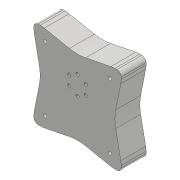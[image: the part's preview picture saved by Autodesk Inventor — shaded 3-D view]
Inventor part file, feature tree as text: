
AUTODESK INVENTOR PART (.ipt)
format: ipt  version: 2018 (Build 220112000, 112)  size: 1,824,768 bytes
history: native  units: mm
features: sketch x42, projected_geometry x36, extrude x34, fillet x9, hole x6, chamfer x5, other x2, pattern_circular x2, mirror x1, revolve x1, shell x1, plane x1, loft x1
ambient origin geometry x8: Origin, YZ Plane, XZ Plane, XY Plane, X Axis, Y Axis, Z Axis, Center Point
bodies: Solid1 (feature_tree), Solid2 (feature_tree)
feature tree (141):
  extrude  "Extrusion1"  Depth=45.0mm
  extrude  "Extrusion2"  Depth=2.25mm
  hole  "Hole1"  [1 undecoded]
  hole  "Hole2"  [1 undecoded]
  fillet  "Fillet1"  Radius=14.0mm
  extrude  "Extrusion3"  Depth=18.5mm
  extrude  "Extrusion4"  Depth=10.0mm
  extrude  "Extrusion5"  Depth=2.195mm
  extrude  "Extrusion6"  Depth=20.5mm
  hole  "Hole3"  [1 undecoded]
  extrude  "Extrusion7"  Depth=0.5mm
  extrude  "Extrusion8"  Depth=5.0mm TaperAngle=0.0deg
  extrude  "Extrusion9"  Depth=10.0mm
  extrude  "Extrusion10"  Depth=10.0mm
  extrude  "Extrusion11"  Depth=14.5mm
  extrude  "Extrusion12"  Depth=14.5mm
  extrude  "Extrusion13"  Depth=5.0mm
  extrude  "Extrusion14"  Depth=2.25mm
  extrude  "Extrusion15"  Depth=5.0mm
  extrude  "Extrusion16"  Depth=9.0mm
  extrude  "Extrusion17"  Depth=4.0mm
  chamfer  "Chamfer1"  Distance=1.0mm
  fillet  "Fillet7"  Radius=20.7mm
  fillet  "Fillet8"  Radius=32.0mm
  mirror  "Mirror1"
  extrude  "Extrusion18"  Depth=1.0mm TaperAngle=0.0deg
  extrude  "Extrusion19"  Depth=8.0mm
  extrude  "Extrusion20"  Depth=0.2mm TaperAngle=0.0deg
  extrude  "Extrusion21"  Depth=0.5mm TaperAngle=0.0deg
  extrude  "Extrusion22"  Depth=3.0mm TaperAngle=0.0deg
  extrude  "Extrusion23"  Depth=0.2mm TaperAngle=0.0deg
  extrude  "Extrusion24"  Depth=2.5mm TaperAngle=45.0deg
  sketch  "Sketch35"  dims[d91=8.0mm d92=0.0mm d93=3.0mm d94=0.0mm]
  other  "Work Axis1"
  revolve  "Revolution1"  [1 undecoded]
  extrude  "Extrusion25"  Depth=4.0mm TaperAngle=0.0deg
  extrude  "Extrusion26"  Depth=19.2mm TaperAngle=0.0deg
  shell  "Shell1"  Thickness=52.1mm
  extrude  "Extrusion27"  Depth=9.0mm
  extrude  "Extrusion28"  Depth=25.0mm
  chamfer  "Chamfer4"  Distance=6.9mm
  chamfer  "Chamfer5"  Distance=2.5mm
  extrude  "Extrusion29"  TaperAngle=90.0deg  [1 undecoded]
  pattern_circular  "Circular Pattern1"  [2 undecoded]
  fillet  "Fillet11"  Radius=5.0mm
  fillet  "Fillet12"  Radius=12.8mm
  fillet  "Fillet13"  Radius=12.8mm
  fillet  "Fillet14"  Radius=12.8mm
  chamfer  "Chamfer6"  Distance=12.8mm
  hole  "Hole6"  [1 undecoded]
  extrude  "Extrusion30"  Depth=25.0mm
  fillet  "Fillet15"  Radius=20.0mm
  extrude  "Extrusion31"  Depth=25.0mm
  plane  "Work Plane1"
  loft  "Loft1"
  hole  "Hole8"  [1 undecoded]
  extrude  "Extrusion35"  Depth=25.0mm TaperAngle=0.0deg
  chamfer  "Chamfer7"  Distance=40.0mm
  fillet  "Fillet20"  Radius=5.1mm
  extrude  "Extrusion36"  Depth=25.0mm TaperAngle=45.0deg
  extrude  "Extrusion37"  Depth=10.0mm
  hole  "Hole9"  [1 undecoded]
  pattern_circular  "Circular Pattern2"  Count=4  [1 undecoded]
  sketch  "Sketch1"  dims[d0=24.5mm d1=45.0mm]
  sketch  "Sketch2"  dims[d2=1.95mm d3=0.0mm d4=2.25mm]
  projected_geometry  "Projected Loop1"
  sketch  "Sketch3"  dims[d5=20.0mm d6=2.25mm]
  projected_geometry  "Projected Loop2"
  sketch  "Sketch4"  dims[d7=5.25mm d8=5.25mm d9=14.0mm]
  projected_geometry  "Projected Loop3"
  sketch  "Sketch5"  dims[d10=5.25mm d11=18.5mm]
  projected_geometry  "Projected Loop4"
  sketch  "Sketch6"  dims[d12=10.0mm d13=0.0mm d14=20.5mm]
  projected_geometry  "Projected Loop5"
  sketch  "Sketch7"  dims[d15=2.0mm d16=2.195mm]
  projected_geometry  "Projected Loop6"
  sketch  "Sketch8"  dims[d17=2.0mm]
  projected_geometry  "Projected Loop7"
  sketch  "Sketch9"  dims[d18=2.4mm d19=6.0mm d20=4.4mm d21=2.0mm d22=90.0deg d23=8.0mm d24=20.594885mm d25=20.5mm]
  projected_geometry  "Projected Loop8"
  projected_geometry  "Projected Loop9"
  sketch  "Sketch10"  dims[d26=26.65mm d27=2.0mm]
  projected_geometry  "Projected Loop10"
  projected_geometry  "Projected Loop11"
  sketch  "Sketch11"  dims[d28=2.0mm]
  projected_geometry  "Projected Loop12"
  sketch  "Sketch12"  dims[d29=2.4mm d30=6.0mm d31=4.4mm d32=2.0mm d33=90.0deg d34=8.0mm d35=20.594885mm d36=0.5mm]
  sketch  "Sketch13"  dims[d37=18.0mm d38=5.0mm d39=0.0mm]
  sketch  "Sketch14"  dims[d41=10.0mm d42=0.0mm d43=24.5mm]
  projected_geometry  "Projected Loop13"
  sketch  "Sketch15"  dims[d44=1.15mm d45=0.0mm d46=10.0mm]
  sketch  "Sketch16"  dims[d47=21.0mm d48=14.5mm]
  projected_geometry  "Projected Loop14"
  sketch  "Sketch17"  dims[d49=20.0mm d50=14.5mm]
  projected_geometry  "Projected Loop15"
  sketch  "Sketch18"  dims[d51=24.5mm d52=5.0mm]
  projected_geometry  "Projected Loop16"
  sketch  "Sketch19"  dims[d53=5.0mm d54=2.25mm]
  projected_geometry  "Projected Loop17"
  sketch  "Sketch20"  dims[d55=2.25mm d56=5.0mm]
  projected_geometry  "Projected Loop18"
  sketch  "Sketch22"  dims[d57=5.0mm d58=9.0mm]
  sketch  "Sketch25"  dims[d59=14.75mm d60=4.0mm d61=1.0mm d62=0.0mm d63=20.7mm]
  sketch  "Sketch27"  dims[d64=2.4mm d65=6.0mm d66=4.4mm d67=2.0mm d68=90.0deg d69=8.0mm d70=20.594885mm d72=32.0mm]
  projected_geometry  "Projected Loop22"
  sketch  "Sketch28"  dims[d73=5.0mm d74=0.0mm d75=1.0mm d76=0.0mm]
  projected_geometry  "Projected Loop23"
  sketch  "Sketch29"  dims[d77=12.25mm d78=0.0mm d80=8.0mm]
  projected_geometry  "Projected Loop24"
  sketch  "Sketch30"  dims[d81=4.5mm d82=0.0mm d84=0.2mm d85=0.0mm]
  projected_geometry  "Projected Loop25"
  sketch  "Sketch33"  dims[d86=21.0mm d87=0.5mm d88=0.0mm]
  projected_geometry  "Projected Loop26"
  sketch  "Sketch36"  dims[d95=5.0mm d96=0.0mm d98=0.2mm d99=0.0mm]
  projected_geometry  "Projected Loop27"
  sketch  "Sketch37"  dims[d100=0.2mm d101=0.0mm d102=2.5mm d103=2.0mm d104=45.0deg]
  projected_geometry  "Projected Loop28"
  sketch  "Sketch38"  dims[d105=1.5mm d114=0.5mm]
  projected_geometry  "Projected Loop29"
  projected_geometry  "Projected Loop30"
  projected_geometry  "Projected Loop31"
  projected_geometry  "Projected Loop32"
  sketch  "Sketch39"  dims[d115=22.55mm d116=0.0mm d128=4.0mm d129=0.0mm]
  projected_geometry  "Projected Loop33"
  projected_geometry  "Projected Loop34"
  sketch  "Sketch40"  dims[d130=4.0mm d131=0.0mm d132=19.2mm d133=0.0mm d134=52.1mm]
  projected_geometry  "Projected Loop35"
  sketch  "Sketch41"  dims[d135=6.8mm d136=0.0mm d137=9.0mm]
  projected_geometry  "Projected Loop36"
  sketch  "Sketch42"  dims[d138=9.0mm d139=25.0mm d140=6.9mm d141=0.0mm]
  sketch  "Sketch43"  dims[d142=5.2mm]
  projected_geometry  "Projected Loop37"
  sketch  "Sketch49"  dims[d143=5.2mm]
  other  "Edges1"
  sketch  "Sketch50"  dims[d144=5.2mm]
  sketch  "Sketch51"  dims[d145=5.2mm d146=2.5mm d147=0.0mm]
  sketch  "Sketch52"  dims[d148=5.0mm d149=90.0deg]
  projected_geometry  "Projected Loop40"
  sketch  "Sketch53"  dims[d150=5.0mm]
  sketch  "Sketch54"  dims[d151=105.0mm d152=105.0mm d153=5.0mm d154=0.0mm d156=12.8mm d157=12.8mm d158=12.8mm d159=12.8mm d160=20.0mm d161=20.0mm d162=20.0mm d163=6.0mm d164=40.0mm d165=0.0mm d166=8.0mm d167=40.0mm d168=0.0mm d169=40.0mm d170=0.0mm d178=5.1mm d179=2.45mm d180=45.0deg d181=4.1mm d182=2.45mm d183=45.0deg d184=10.0mm d185=10.0mm d186=40.0mm d187=0.0mm d188=40.0mm d189=360.0deg d191=5.1mm d192=25.0mm d193=50.0mm d194=50.0mm d195=5.0mm d196=2.0mm d197=45.0deg d198=110.0mm d199=77.781746mm d200=77.781746mm d201=4.134mm d202=10.0mm d203=12.6mm d204=2.0mm d205=90.0deg d206=14.2mm d207=20.594885mm d208=11.0mm d209=11.0mm d210=11.0mm d211=11.0mm d212=45.0mm d213=0.0mm d214=1.0mm d215=2.0mm d216=0.0mm d236=45.0mm d237=150.0mm d238=0.0mm d239=90.0deg d240=0.0mm d241=90.0deg d242=4.134mm d243=10.0mm d244=4.0mm d245=2.0mm d246=90.0deg d247=14.2mm d248=20.594885mm d249=45.0mm d250=0.0mm d251=1.0mm d252=2.0mm d253=45.0deg d254=1.0mm d255=30.0mm d256=0.0mm d257=25.0mm d258=0.0mm d259=11.5mm d260=4.134mm d261=20.0mm d262=4.0mm d263=2.0mm d264=90.0deg d265=25.0mm d266=20.594885mm d267=60.0mm d268=360.0deg]
  projected_geometry  "Project Cut Edges1"
note: 11 required parameter values undecoded (feature->parameter linkage not recoverable at this tier; creation-order binding heuristic only, values carry confidence <= 0.55)